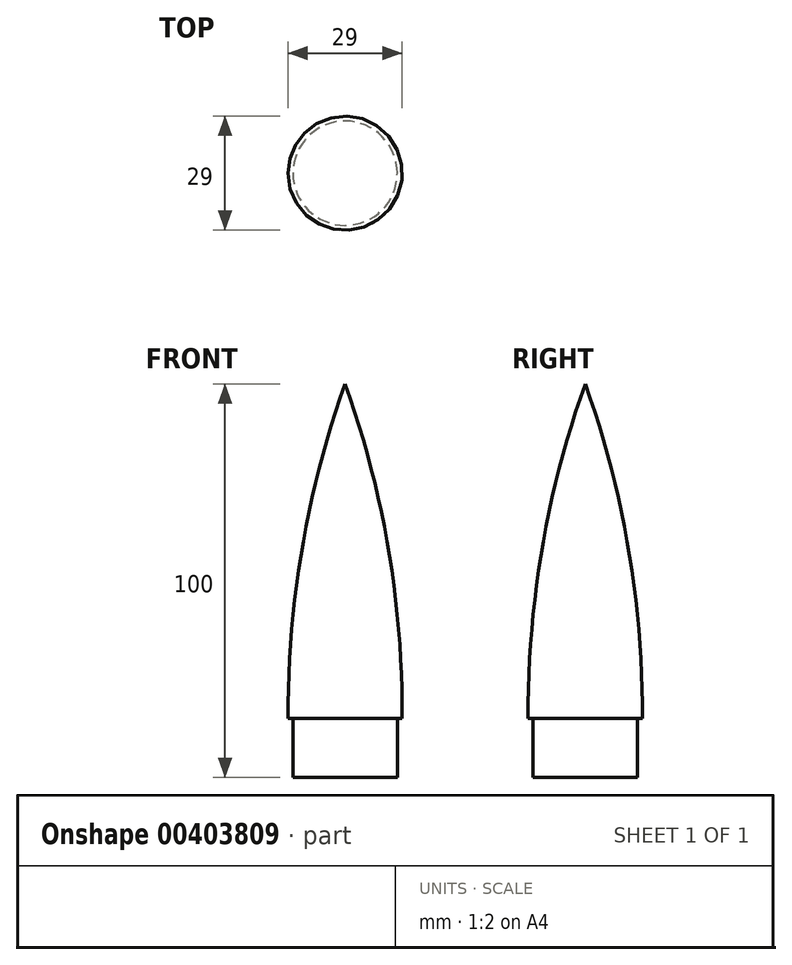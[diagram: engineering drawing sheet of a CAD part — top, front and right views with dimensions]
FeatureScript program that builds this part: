
annotation { "Feature Type Name" : "Feature", "Feature Type Description" : "" }
export const myFeature = defineFeature(function(context is Context, id is Id, definition is map)
    precondition{}
    {
        {
            var Q0;
            Q0=qCreatedBy(makeId("Front.planeOp"),FACE);
            var sketch = newSketch(context, id + "F0", { "sketchPlane" : qUnion([Q0])});
            skLineSegment(sketch, "E0", {"start": v(0, 0) * mm, "end": v(14.5, 0) * mm});
            skLineSegment(sketch, "E1", {"start": v(0, -15) * mm, "end": v(13.25, -15) * mm});
            skLineSegment(sketch, "E2", {"start": v(0, 85) * mm, "end": v(0, -15) * mm});
            skLineSegment(sketch, "E3", {"start": v(13.25, -15) * mm, "end": v(13.25, 0) * mm});
            skArc(sketch, "E4", {"start": v(14.5, 0) * mm, "mid": v(10.96, 43.13) * mm, "end": v(0, 85) * mm});
            skSolve(sketch);
        }
        {
            var Q0;
            {var subQ4=sQuery(id+"F0.wireOp",EDGE,"E4");Q0=makeQuery(id+"F0.imprint","IMPRINT",FACE,{"disambiguationData":[TD([[makeQuery(id+"F0.imprint","IMPRINT",EDGE,{"derivedFrom":subQ4}),1.0]])]});}
            var Q1;
            {var subQ4=sQuery(id+"F0.wireOp",EDGE,"E1");Q1=makeQuery(id+"F0.imprint","IMPRINT",FACE,{"disambiguationData":[TD([[makeQuery(id+"F0.imprint","IMPRINT",EDGE,{"derivedFrom":subQ4}),1.0]])]});}
            var Q2;
            Q2=sQuery(id+"F0.wireOp",EDGE,"E2");
            revolve(context, id + "F1", {"entities" : qUnion([Q0, Q1]), "axis" : qUnion([Q2]), "revolveType" : RevolveType.FULL});
        }
    });
